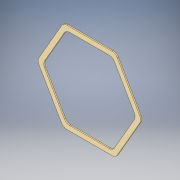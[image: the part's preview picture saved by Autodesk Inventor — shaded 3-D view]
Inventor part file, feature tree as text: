
AUTODESK INVENTOR PART (.ipt)
format: ipt  version: 2019 (Build 230136000, 136)  size: 143,360 bytes
history: native  units: mm
features: extrude x2, fillet x2, sketch x2
ambient origin geometry x8: Origin, YZ Plane, XZ Plane, XY Plane, X Axis, Y Axis, Z Axis, Center Point
bodies: Solid1 (feature_tree)
feature tree (6):
  extrude  "Extrusion1"  Depth=2.0mm TaperAngle=0.0deg
  extrude  "Extrusion6"  Depth=10.0mm TaperAngle=0.0deg
  fillet  "Fillet2"  Radius=10.0mm
  fillet  "Fillet3"  Radius=10.0mm
  sketch  "Sketch1"  dims[d0=150.0mm d1=2.0mm d2=0.0mm]
  sketch  "Sketch7"  dims[d19=4.0mm d20=7.0mm d21=0.0mm d24=10.0mm d25=10.0mm]
